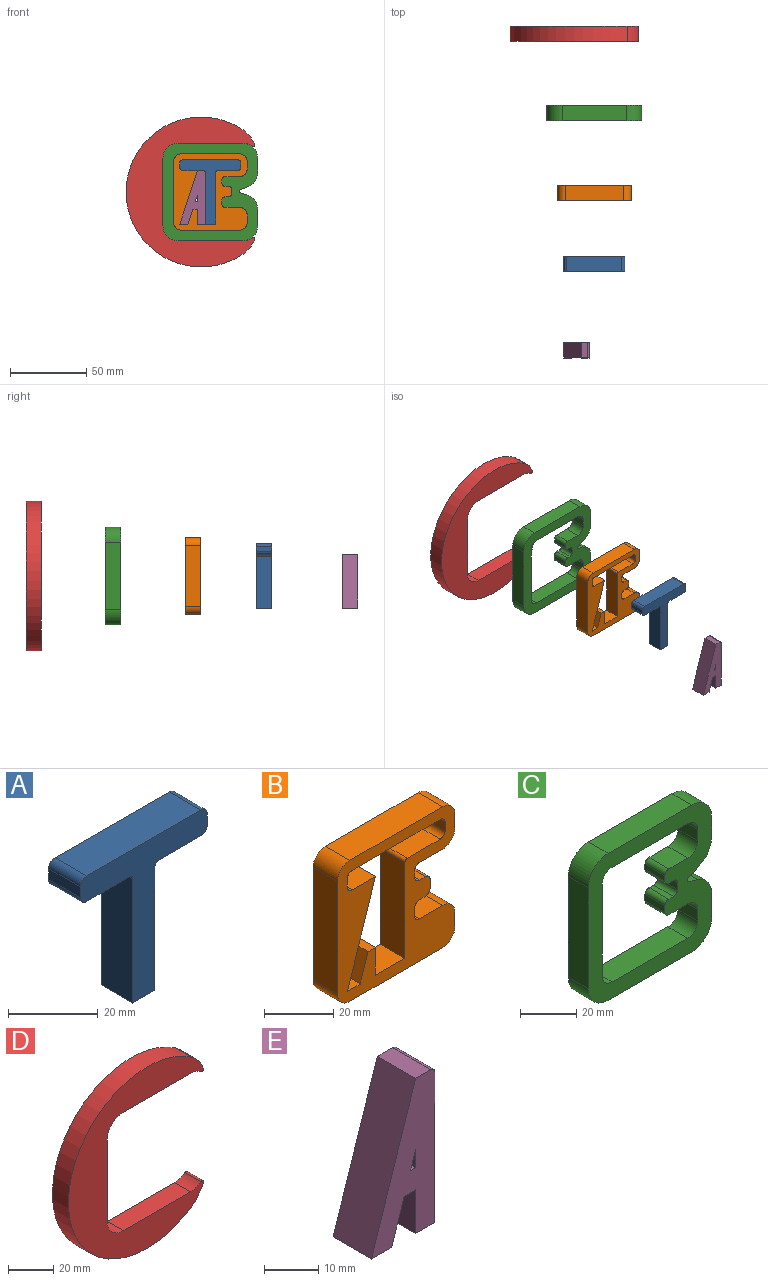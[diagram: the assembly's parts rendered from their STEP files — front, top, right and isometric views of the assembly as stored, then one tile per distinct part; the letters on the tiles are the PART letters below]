
ASSEMBLY  parts=5 mates=9
PART A: 16 faces, bbox 40x10x42 mm
  f0: plane 13.5x10mm, normal (0,0,-1), area 135mm2, adj f8,f9,f10,f15
  f1: plane 10x3mm, normal (1,0,0), area 30mm2, adj f8,f9,f10,f11
  f2: plane 36x10mm, normal (0,0,1), area 360mm2, adj f8,f9,f11,f12
  f3: plane 10x2.96mm, normal (-1,0,0), area 29.6mm2, adj f8,f9,f12,f13
  f4: plane 13.5x10mm, normal (0,0,-1), area 135mm2, adj f8,f9,f13,f14
  f5: plane 34x10mm, normal (-1,0,0), area 340mm2, adj f6,f8,f9,f14
  f6: plane 10x7mm, normal (0,0,-1), area 70mm2, adj f5,f7,f8,f9
  f7: plane 33.96x10mm, normal (1,0,0), area 339.6mm2, adj f6,f8,f9,f15
  f8: plane 41.96x40mm, normal (0,-1,0), area 521mm2, adj f0,f1,f2,f3,f4,f5,f6,f7
  f9: plane 41.96x40mm, normal (0,1,0), area 521mm2, adj f0,f1,f2,f3,f4,f5,f6,f7
  f10: cylinder r=2mm len=10mm, axis (0,-1,0), area 31.4mm2, adj f0,f1,f8,f9
  f11: cylinder r=2mm len=10mm, axis (0,1,0), area 31.4mm2, adj f1,f2,f8,f9
  f12: cylinder r=2mm len=10mm, axis (0,1,0), area 31.4mm2, adj f2,f3,f8,f9
  f13: cylinder r=2mm len=10mm, axis (0,1,0), area 31.4mm2, adj f3,f4,f8,f9
  f14: cylinder r=1mm len=10mm, axis (0,1,0), area 15.7mm2, adj f4,f5,f8,f9
  f15: cylinder r=1mm len=10mm, axis (0,-1,0), area 15.7mm2, adj f0,f7,f8,f9
PART B: 43 faces, bbox 48x10x50 mm
  f0: plane 10x9.5mm, normal (0,0,-1), area 95mm2, adj f24,f25,f30,f41
  f1: plane 10x5mm, normal (1,0,0), area 50mm2, adj f24,f25,f30,f31
  f2: plane 38x10mm, normal (0,0,1), area 380mm2, adj f24,f25,f31,f32
  f3: plane 39.96x10mm, normal (-1,0,0), area 399.6mm2, adj f24,f25,f32,f33
  f4: plane 38x10mm, normal (0,0,-1), area 380mm2, adj f24,f25,f33,f34
  f5: plane 10x5mm, normal (1,0,0), area 50mm2, adj f24,f25,f34,f35
  f6: plane 10x9.5mm, normal (0,0,1), area 95mm2, adj f24,f25,f35,f36
  f7: plane 10x2.75mm, normal (1,0,0), area 27.5mm2, adj f24,f25,f36,f37
  f8: plane 10x2.35mm, normal (0,0,-1), area 23.5mm2, adj f24,f25,f37,f38
  f9: plane 10x3mm, normal (1,0,0), area 30mm2, adj f24,f25,f38,f39
  f10: plane 10x2.35mm, normal (0,0,1), area 23.5mm2, adj f24,f25,f39,f40
  f11: plane 10x3mm, normal (-1,0,0), area 30mm2, adj f24,f25,f26,f29
  f12: plane 13.5x10mm, normal (0,0,1), area 135mm2, adj f24,f25,f26,f42
  f13: plane 33.96x10mm, normal (-1,0,0), area 339.6mm2, adj f14,f24,f25,f42
  f14: plane 12x10mm, normal (0,0,1), area 120mm2, adj f13,f15,f24,f25
  f15: plane 10x9.86mm, normal (1,0,0), area 98.6mm2, adj f14,f16,f24,f25
  f16: plane 10x3mm, normal (0,0,1), area 30mm2, adj f15,f17,f24,f25
  f17: plane 10x9.86mm, normal (-0.95,0,0.31), area 103.8mm2, adj f16,f18,f24,f25
  f18: plane 10x5.26mm, normal (0,0,1), area 52.6mm2, adj f17,f19,f24,f25
  f19: plane 35x11.5mm, normal (0.95,0,-0.31), area 368.4mm2, adj f18,f20,f24,f25
  f20: plane 10x9.5mm, normal (0,0,1), area 95mm2, adj f19,f24,f25,f27
  f21: plane 10x2.96mm, normal (1,0,0), area 29.6mm2, adj f24,f25,f27,f28
  f22: plane 36x10mm, normal (0,0,-1), area 360mm2, adj f24,f25,f28,f29
  f23: plane 10x2.2mm, normal (1,0,0), area 22mm2, adj f24,f25,f40,f41
  f24: plane 49.96x48mm, normal (0,-1,0), area 1231.1mm2, adj f0,f1,f2,f3,f4,f5,f6,f7
  f25: plane 49.96x48mm, normal (0,1,0), area 1231.1mm2, adj f0,f1,f2,f3,f4,f5,f6,f7
  f26: cylinder r=2mm len=10mm, axis (0,1,0), area 31.4mm2, adj f11,f12,f24,f25
  f27: cylinder r=2mm len=10mm, axis (0,-1,0), area 31.4mm2, adj f20,f21,f24,f25
  f28: cylinder r=2mm len=10mm, axis (0,-1,0), area 31.4mm2, adj f21,f22,f24,f25
  f29: cylinder r=2mm len=10mm, axis (0,-1,0), area 31.4mm2, adj f11,f22,f24,f25
  f30: cylinder r=5mm len=10mm, axis (0,1,0), area 78.5mm2, adj f0,f1,f24,f25
  f31: cylinder r=5mm len=10mm, axis (0,1,0), area 78.5mm2, adj f1,f2,f24,f25
  f32: cylinder r=5mm len=10mm, axis (0,1,0), area 78.5mm2, adj f2,f3,f24,f25
  f33: cylinder r=5mm len=10mm, axis (0,1,0), area 78.5mm2, adj f3,f4,f24,f25
  f34: cylinder r=5mm len=10mm, axis (0,1,0), area 78.5mm2, adj f4,f5,f24,f25
  f35: cylinder r=5mm len=10mm, axis (0,1,0), area 78.5mm2, adj f5,f6,f24,f25
  f36: cylinder r=2mm len=10mm, axis (0,-1,0), area 31.4mm2, adj f6,f7,f24,f25
  f37: cylinder r=2mm len=10mm, axis (0,-1,0), area 31.4mm2, adj f7,f8,f24,f25
  f38: cylinder r=2mm len=10mm, axis (0,1,0), area 31.4mm2, adj f8,f9,f24,f25
  f39: cylinder r=2mm len=10mm, axis (0,1,0), area 31.4mm2, adj f9,f10,f24,f25
  f40: cylinder r=2mm len=10mm, axis (0,-1,0), area 31.4mm2, adj f10,f23,f24,f25
  f41: cylinder r=2mm len=10mm, axis (0,-1,0), area 31.4mm2, adj f0,f23,f24,f25
  f42: cylinder r=1mm len=10mm, axis (0,1,0), area 15.7mm2, adj f12,f13,f24,f25
PART C: 40 faces, bbox 62x10x64 mm
  f0: plane 10x5mm, normal (-1,0,0), area 50mm2, adj f19,f20,f21,f26
  f1: plane 10x9.5mm, normal (0,0,1), area 95mm2, adj f19,f20,f21,f27
  f2: plane 10x2.2mm, normal (-1,0,0), area 22mm2, adj f19,f20,f27,f28
  f3: plane 10x2.35mm, normal (0,0,-1), area 23.5mm2, adj f19,f20,f28,f29
  f4: plane 10x3mm, normal (-1,0,0), area 30mm2, adj f19,f20,f29,f30
  f5: plane 10x2.35mm, normal (0,0,1), area 23.5mm2, adj f19,f20,f30,f31
  f6: plane 10x2.75mm, normal (-1,0,0), area 27.5mm2, adj f19,f20,f31,f32
  f7: plane 10x9.5mm, normal (0,0,-1), area 95mm2, adj f19,f20,f22,f32
  f8: plane 10x5mm, normal (-1,0,0), area 50mm2, adj f19,f20,f22,f23
  f9: plane 38x10mm, normal (0,0,1), area 380mm2, adj f19,f20,f23,f24
  f10: plane 39.96x10mm, normal (1,0,0), area 399.6mm2, adj f19,f20,f24,f25
  f11: plane 42x10mm, normal (0,0,-1), area 420mm2, adj f19,f20,f33,f39
  f12: plane 10.55x10mm, normal (1,0,0), area 105.5mm2, adj f19,f20,f33,f34
  f13: plane 10x4.42mm, normal (0.29,0,0.96), area 46.2mm2, adj f19,f20,f34,f37
  f14: plane 10x5.65mm, normal (0.4,0,-0.91), area 61.8mm2, adj f19,f20,f35,f37
  f15: plane 10x8.97mm, normal (1,0,0), area 89.7mm2, adj f19,f20,f35,f36
  f16: plane 42x10mm, normal (0,0,1), area 420mm2, adj f19,f20,f36,f38
  f17: plane 43.96x10mm, normal (-1,0,0), area 439.6mm2, adj f19,f20,f38,f39
  f18: plane 38x10mm, normal (0,0,-1), area 380mm2, adj f19,f20,f25,f26
  f19: plane 63.96x62mm, normal (0,-1,0), area 1706.6mm2, adj f0,f1,f2,f3,f4,f5,f6,f7
  f20: plane 63.96x62mm, normal (0,1,0), area 1706.6mm2, adj f0,f1,f2,f3,f4,f5,f6,f7
  f21: cylinder r=5mm len=10mm, axis (0,-1,0), area 78.5mm2, adj f0,f1,f19,f20
  f22: cylinder r=5mm len=10mm, axis (0,-1,0), area 78.5mm2, adj f7,f8,f19,f20
  f23: cylinder r=5mm len=10mm, axis (0,-1,0), area 78.5mm2, adj f8,f9,f19,f20
  f24: cylinder r=5mm len=10mm, axis (0,-1,0), area 78.5mm2, adj f9,f10,f19,f20
  f25: cylinder r=5mm len=10mm, axis (0,-1,0), area 78.5mm2, adj f10,f18,f19,f20
  f26: cylinder r=5mm len=10mm, axis (0,-1,0), area 78.5mm2, adj f0,f18,f19,f20
  f27: cylinder r=2mm len=10mm, axis (0,1,0), area 31.4mm2, adj f1,f2,f19,f20
  f28: cylinder r=2mm len=10mm, axis (0,1,0), area 31.4mm2, adj f2,f3,f19,f20
  f29: cylinder r=2mm len=10mm, axis (0,-1,0), area 31.4mm2, adj f3,f4,f19,f20
  f30: cylinder r=2mm len=10mm, axis (0,-1,0), area 31.4mm2, adj f4,f5,f19,f20
  f31: cylinder r=2mm len=10mm, axis (0,1,0), area 31.4mm2, adj f5,f6,f19,f20
  f32: cylinder r=2mm len=10mm, axis (0,1,0), area 31.4mm2, adj f6,f7,f19,f20
  f33: cylinder r=10mm len=10mm, axis (0,1,0), area 157.1mm2, adj f11,f12,f19,f20
  f34: cylinder r=10mm len=10mm, axis (0,1,0), area 127.4mm2, adj f12,f13,f19,f20
  f35: cylinder r=10mm len=10mm, axis (0,1,0), area 115.4mm2, adj f14,f15,f19,f20
  f36: cylinder r=10mm len=10mm, axis (0,1,0), area 157.1mm2, adj f15,f16,f19,f20
  f37: cylinder r=1mm len=10mm, axis (0,-1,0), area 24.3mm2, adj f13,f14,f19,f20
  f38: cylinder r=10mm len=10mm, axis (0,1,0), area 157.1mm2, adj f16,f17,f19,f20
  f39: cylinder r=10mm len=10mm, axis (0,1,0), area 157.1mm2, adj f11,f17,f19,f20
PART D: 14 faces, bbox 84.2x10x98 mm
  f0: cylinder r=49mm len=98mm, axis (0,1,0), area 2124.2mm2, adj f6,f7,f10,f11
  f1: cylinder r=10mm len=10mm, axis (0,1,0), area 69.5mm2, adj f2,f6,f7,f12
  f2: plane 42x10mm, normal (0,0,1), area 420mm2, adj f1,f6,f7,f8
  f3: plane 43.96x10mm, normal (1,0,0), area 439.6mm2, adj f6,f7,f8,f9
  f4: plane 42x10mm, normal (0,0,-1), area 420mm2, adj f5,f6,f7,f9
  f5: cylinder r=10mm len=10mm, axis (0,1,0), area 69.5mm2, adj f4,f6,f7,f13
  f6: plane 98x84.17mm, normal (0,-1,0), area 3100.3mm2, adj f0,f1,f2,f3,f4,f5,f8,f9
  f7: plane 98x84.17mm, normal (0,1,0), area 3100.3mm2, adj f0,f1,f2,f3,f4,f5,f8,f9
  f8: cylinder r=10mm len=10mm, axis (0,-1,0), area 157.1mm2, adj f2,f3,f6,f7
  f9: cylinder r=10mm len=10mm, axis (0,-1,0), area 157.1mm2, adj f3,f4,f6,f7
  f10: cylinder r=20mm len=10mm, axis (0,1,0), area 125.7mm2, adj f0,f6,f7,f13
  f11: cylinder r=20mm len=10mm, axis (0,1,0), area 125.7mm2, adj f0,f6,f7,f12
  f12: cylinder r=1mm len=10mm, axis (0,-1,0), area 26.1mm2, adj f1,f6,f7,f11
  f13: cylinder r=1mm len=10mm, axis (0,-1,0), area 26.1mm2, adj f5,f6,f7,f10
PART E: 14 faces, bbox 16.5x10x35 mm
  f0: plane 10x9.86mm, normal (-1,0,0), area 98.6mm2, adj f1,f10,f11,f12
  f1: plane 10x5mm, normal (0,0,-1), area 50mm2, adj f0,f2,f11,f12
  f2: plane 34x10mm, normal (1,0,0), area 340mm2, adj f1,f11,f12,f13
  f3: plane 10x4mm, normal (0,0,1), area 40mm2, adj f4,f11,f12,f13
  f4: plane 35x11.5mm, normal (-0.95,0,0.31), area 368.4mm2, adj f3,f5,f11,f12
  f5: plane 10x5.26mm, normal (0,0,-1), area 52.6mm2, adj f4,f6,f11,f12
  f6: plane 10x9.86mm, normal (0.95,0,-0.31), area 103.8mm2, adj f5,f10,f11,f12
  f7: plane 10x1.35mm, normal (0,0,1), area 13.5mm2, adj f8,f9,f11,f12
  f8: plane 10x4.12mm, normal (0.95,0,-0.31), area 43.4mm2, adj f7,f9,f11,f12
  f9: plane 10x4.12mm, normal (-1,0,0), area 41.2mm2, adj f7,f8,f11,f12
  f10: plane 10x3mm, normal (0,0,-1), area 30mm2, adj f0,f6,f11,f12
  f11: plane 35x16.5mm, normal (0,-1,0), area 327.7mm2, adj f0,f1,f2,f3,f4,f5,f6,f7
  f12: plane 35x16.5mm, normal (0,1,0), area 327.7mm2, adj f0,f1,f2,f3,f4,f5,f6,f7
  f13: cylinder r=1mm len=10mm, axis (0,1,0), area 15.7mm2, adj f2,f3,f11,f12
PLACE A t=(-39.31,-168.34,6.04)mm
PLACE B t=(-39.31,-121.77,6.04)mm
PLACE C t=(-39.31,-69.58,6.04)mm
PLACE D t=(-39.31,-17.74,6.04)mm fixed
PLACE E t=(-39.31,-224.65,6.04)mm
MATE planar A.f2 <-> B.f22  axis (0,0,1) through (-35.81,-173.34,29.18)mm
MATE planar E.f2 <-> A.f5  axis (1,0,0) through (-39.31,-229.65,4.22)mm
MATE planar A.f7 <-> B.f13  axis (1,0,0) through (-32.31,-178.34,4.2)mm
MATE planar C.f17 <-> D.f3  axis (-1,0,0) through (-66.81,-74.58,8.2)mm
MATE planar B.f3 <-> C.f10  axis (-1,0,0) through (-59.81,-131.77,8.2)mm
MATE planar C.f11 <-> D.f2  axis (0,0,-1) through (-14.81,-74.58,-23.78)mm
MATE planar B.f4 <-> C.f9  axis (0,0,-1) through (-35.81,-126.77,-16.78)mm
MATE planar E.f1 <-> B.f14  axis (0,0,-1) through (-41.81,-229.65,-12.78)mm
MATE planar A.f6 <-> B.f14  axis (0,0,-1) through (-35.81,-173.34,-12.78)mm
